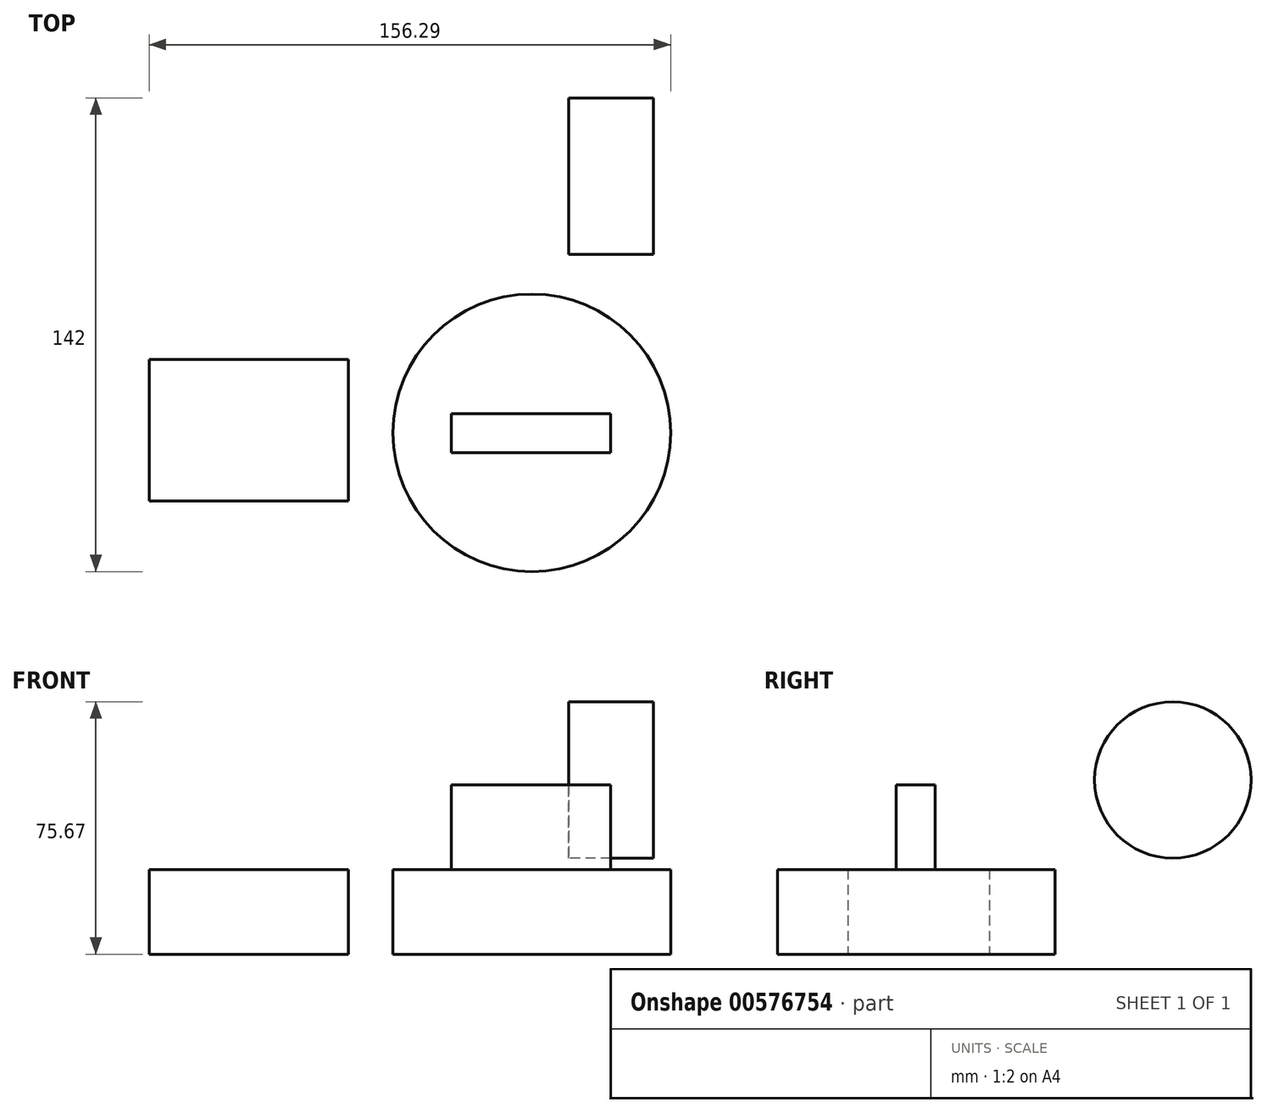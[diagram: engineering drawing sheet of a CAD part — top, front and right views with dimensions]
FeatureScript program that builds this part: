
annotation { "Feature Type Name" : "Feature", "Feature Type Description" : "" }
export const myFeature = defineFeature(function(context is Context, id is Id, definition is map)
    precondition{}
    {
        {
            var Q0;
            Q0=qCreatedBy(makeId("Top.planeOp"),FACE);
            var sketch = newSketch(context, id + "F0", { "sketchPlane" : qUnion([Q0])});
            skCircle(sketch, "E0", {"center": v(-10.99, 5.94) * mm, "radius": 41.6 * mm});
            skLineSegment(sketch, "E1.bottom", {"start": v(-125.68, 27.89) * mm, "end": v(-65.96, 27.89) * mm});
            skLineSegment(sketch, "E1.top", {"start": v(-125.68, -14.47) * mm, "end": v(-65.96, -14.47) * mm});
            skLineSegment(sketch, "E1.left", {"start": v(-125.68, 27.89) * mm, "end": v(-125.68, -14.47) * mm});
            skLineSegment(sketch, "E1.right", {"start": v(-65.96, 27.89) * mm, "end": v(-65.96, -14.47) * mm});
            skSolve(sketch);
        }
        {
            var Q0;
            Q0 = qSketchRegion(id + "F0", true);
            extrude(context, id + "F1", {"entities" : qUnion([Q0]), "depth" : 25.4 * mm, "offsetDistance" : 25.4 * mm});
        }
        {
            var Q0;
            Q0=qCreatedBy(makeId("Right.planeOp"),FACE);
            var sketch = newSketch(context, id + "F2", { "sketchPlane" : qUnion([Q0])});
            skCircle(sketch, "E2", {"center": v(82.9, 52.23) * mm, "radius": 23.44 * mm});
            skSolve(sketch);
        }
        {
            var Q0;
            Q0 = qSketchRegion(id + "F2", true);
            extrude(context, id + "F3", {"entities" : qUnion([Q0]), "depth" : 25.4 * mm, "offsetDistance" : 25.4 * mm});
        }
        {
            var Q0;
            Q0=makeQuery(id+"F1.opExtrude","CAP_FACE",FACE,{"disambiguationData":[OSD([sQuery(id+"F0.wireOp",EDGE,"E0")])],"isStart":false});
            var sketch = newSketch(context, id + "F4", { "sketchPlane" : qUnion([Q0])});
            skLineSegment(sketch, "E3.bottom", {"start": v(-35.1, 11.64) * mm, "end": v(12.69, 11.64) * mm});
            skLineSegment(sketch, "E3.top", {"start": v(-35.1, 0) * mm, "end": v(12.69, 0) * mm});
            skLineSegment(sketch, "E3.left", {"start": v(-35.1, 11.64) * mm, "end": v(-35.1, 0) * mm});
            skLineSegment(sketch, "E3.right", {"start": v(12.69, 11.64) * mm, "end": v(12.69, 0) * mm});
            skSolve(sketch);
        }
        {
            var Q0;
            Q0=makeQuery(id+"F4.imprint","IMPRINT",FACE,{"disambiguationData":[TD([[makeQuery(id+"F4.imprint","IMPRINT",EDGE,{"derivedFrom":sQuery(id+"F4.wireOp",EDGE,"E3.bottom")}),-1.0]])]});
            extrude(context, id + "F5", {"entities" : qUnion([Q0]), "operationType" : NewBodyOperationType.ADD, "depth" : 25.4 * mm, "offsetDistance" : 25.4 * mm});
        }
    });
